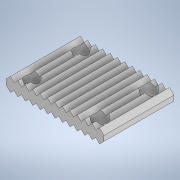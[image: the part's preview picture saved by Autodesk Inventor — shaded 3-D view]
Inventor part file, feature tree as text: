
AUTODESK INVENTOR PART (.ipt)
format: ipt  version: 2020 (Build 240168000, 168)  size: 236,032 bytes
history: native  units: in
note: dims shown in document units (in); Inventor stores cm internally (conversion verified against a paired STEP export)
features: extrude x3, sketch x3, mirror x1
ambient origin geometry x8: Origin, YZ Plane, XZ Plane, XY Plane, X Axis, Y Axis, Z Axis, Center Point
bodies: Solid1 (feature_tree)
feature tree (7):
  extrude  "Extrusion1"  Depth=0.7874in
  extrude  "Extrusion2"  Depth=0.5512in
  mirror  "Mirror1"
  extrude  "Extrusion4"  TaperAngle=135.0deg  [1 undecoded]
  sketch  "Sketch1"  dims[d0=1.1024in d1=0.7874in]
  sketch  "Sketch2"  dims[d2=0.1575in d3=0.0in d4=0.5512in]
  sketch  "Sketch4"  dims[d5=0.0591in d6=135.0deg d7=0.0591in d8=1.9685in d9=0.0in d14=0.1575in d15=0.1575in d16=0.1575in d17=0.1575in d18=0.2362in d19=0.0in]
note: 1 required parameter value undecoded (feature->parameter linkage not recoverable at this tier; creation-order binding heuristic only, values carry confidence <= 0.55)
